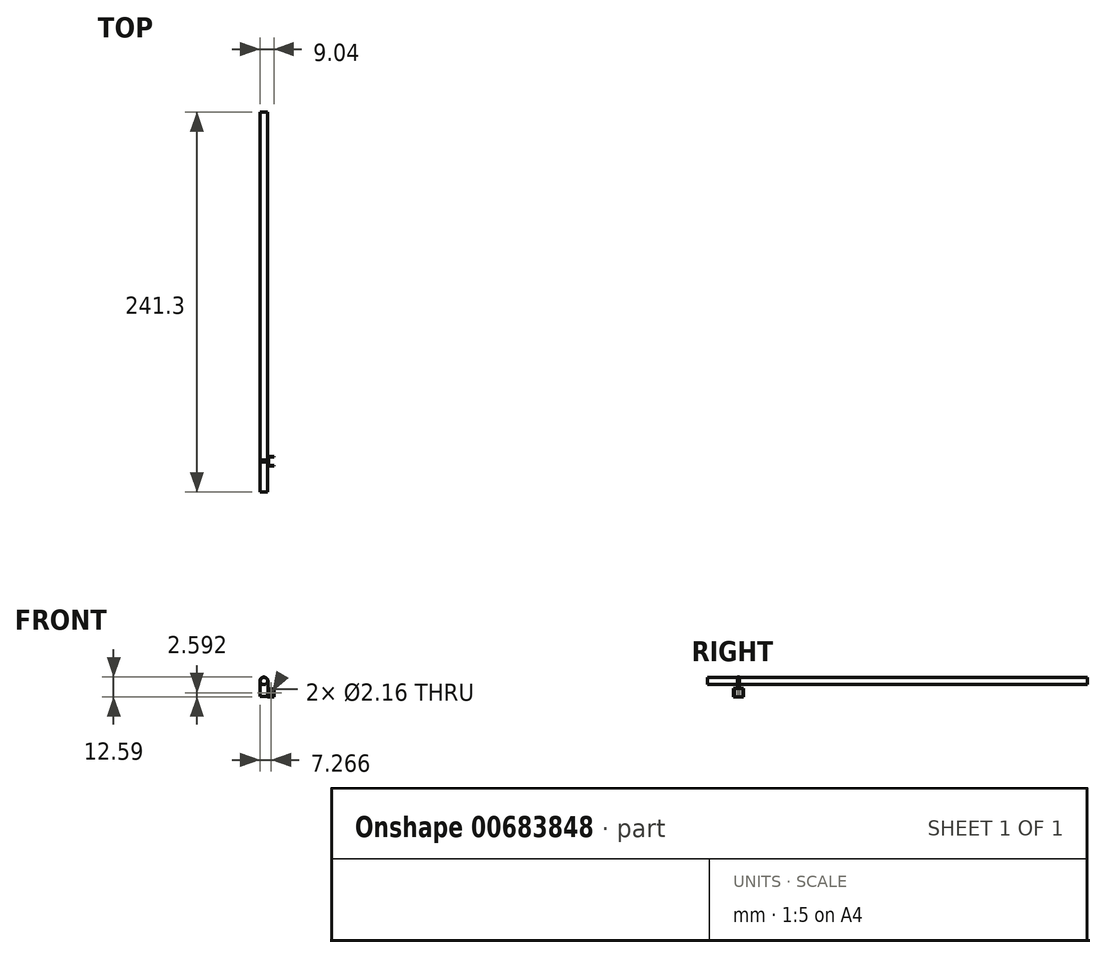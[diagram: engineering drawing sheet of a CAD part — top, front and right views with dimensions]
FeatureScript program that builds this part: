
annotation { "Feature Type Name" : "Feature", "Feature Type Description" : "" }
export const myFeature = defineFeature(function(context is Context, id is Id, definition is map)
    precondition{}
    {
        {
            var Q0;
            Q0=qCreatedBy(makeId("Front.planeOp"),FACE);
            var sketch = newSketch(context, id + "F0", { "sketchPlane" : qUnion([Q0])});
            skCircle(sketch, "E0", {"center": v(0, 5.4) * mm, "radius": 2.56 * mm});
            skArc(sketch, "E1", {"start": v(0, 2.56) * mm, "mid": v(-0.36, 2.53) * mm, "end": v(-0.72, 2.45) * mm});
            skLineSegment(sketch, "E2", {"start": v(2.56, 5.4) * mm, "end": v(2.56, 1.72) * mm});
            skLineSegment(sketch, "E3", {"start": v(-2.56, 5.4) * mm, "end": v(-2.56, 4.38) * mm});
            skArc(sketch, "E4.MirrorC", {"start": v(-11.6, 2.55) * mm, "mid": v(-11.6, 2.55) * mm, "end": v(-11.6, 2.55) * mm});
            skPoint(sketch, "E5.start.orphan", {"position": v(0, -2.56) * mm});
            skPoint(sketch, "E6.start.orphan", {"position": v(0, 2.56) * mm});
            skPoint(sketch, "E7.orphan", {"position": v(2.56, 0) * mm});
            skPoint(sketch, "E8.orphan", {"position": v(-2.56, 0) * mm});
            skLineSegment(sketch, "E9", {"start": v(-2.56, 4.38) * mm, "end": v(-2.56, -2.83) * mm});
            skLineSegment(sketch, "E10", {"start": v(2.56, 1.72) * mm, "end": v(2.52, -2.83) * mm});
            skPoint(sketch, "E10.endSnap0", {"position": v(2.44, 0.77) * mm});
            skPoint(sketch, "E11.start.orphan", {"position": v(2.56, 4.18) * mm});
            skLineSegment(sketch, "E12", {"start": v(-2.56, 5.4) * mm, "end": v(-2.56, -2.83) * mm});
            skPoint(sketch, "E13.end.orphan", {"position": v(2.44, -13.4) * mm});
            skLineSegment(sketch, "E14", {"start": v(-2.56, -2.83) * mm, "end": v(-2.56, -4.37) * mm});
            skLineSegment(sketch, "E15", {"start": v(2.52, -2.83) * mm, "end": v(2.52, -4.37) * mm});
            skLineSegment(sketch, "E16", {"start": v(-2.56, -4.37) * mm, "end": v(2.52, -4.37) * mm});
            skSolve(sketch);
        }
        {
            var Q0;
            {var subQ0=sQuery(id+"F0.wireOp",EDGE,"E0");var subQ1=makeQuery(id+"F0.imprint","INTERSECT",VERTEX,{"derivedFrom":[subQ0,sQuery(id+"F0.wireOp",EDGE,"E2")]});Q0=makeQuery(id+"F0.imprint","IMPRINT",FACE,{"disambiguationData":[TD([[makeQuery(id+"F0.imprint","IMPRINT",EDGE,{"disambiguationData":[TD([[subQ1,1.0]])],"derivedFrom":subQ0}),1.0]])]});}
            var Q1;
            {var subQ0=sQuery(id+"F0.wireOp",EDGE,"E3");Q1=makeQuery(id+"F0.imprint","IMPRINT",FACE,{"disambiguationData":[TD([[makeQuery(id+"F0.imprint","IMPRINT",EDGE,{"derivedFrom":subQ0}),1.0]])]});}
            var Q2;
            {var subQ0=sQuery(id+"F0.wireOp",EDGE,"E2");var subQ1=sQuery(id+"F0.wireOp",EDGE,"E1");var subQ2=makeQuery(id+"F0.imprint","INTERSECT",VERTEX,{"derivedFrom":[subQ1,subQ0]});Q2=makeQuery(id+"F0.imprint","IMPRINT",FACE,{"disambiguationData":[TD([[makeQuery(id+"F0.imprint","IMPRINT",EDGE,{"disambiguationData":[TD([[subQ2,-1.0]])],"derivedFrom":subQ1}),-1.0]])]});}
            var Q3;
            {var subQ0=sQuery(id+"F0.wireOp",EDGE,"E1");var subQ1=makeQuery(id+"F0.imprint","INTERSECT",VERTEX,{"derivedFrom":[subQ0,sQuery(id+"F0.wireOp",EDGE,"E3")]});Q3=makeQuery(id+"F0.imprint","IMPRINT",FACE,{"disambiguationData":[TD([[makeQuery(id+"F0.imprint","IMPRINT",EDGE,{"disambiguationData":[TD([[subQ1,1.0]])],"derivedFrom":subQ0}),1.0]])]});}
            var Q4;
            {var subQ0=sQuery(id+"F0.wireOp",EDGE,"263fcdb8-d820-4d45-9f7c-0084accf3f070.MirrorCS");Q4=makeQuery(id+"F0.imprint","IMPRINT",FACE,{"disambiguationData":[TD([[makeQuery(id+"F0.imprint","IMPRINT",EDGE,{"derivedFrom":subQ0}),1.0]])]});}
            var Q5;
            {var subQ0=sQuery(id+"F0.wireOp",EDGE,"nn3kji8N-mWU8-6sac-MlCo-DN8aCnxxy875");Q5=makeQuery(id+"F0.imprint","IMPRINT",FACE,{"disambiguationData":[TD([[makeQuery(id+"F0.imprint","IMPRINT",EDGE,{"derivedFrom":subQ0}),-1.0]])]});}
            var Q6;
            {var subQ1=sQuery(id+"F0.wireOp",EDGE,"nn3kji8N-mWU8-6sac-MlCo-DN8aCnxxy875");Q6=makeQuery(id+"F0.imprint","IMPRINT",FACE,{"disambiguationData":[TD([[makeQuery(id+"F0.imprint","IMPRINT",EDGE,{"derivedFrom":subQ1}),1.0]])]});}
            var Q7;
            {var subQ0=sQuery(id+"F0.wireOp",EDGE,"G4lSKCHw-J7V3-nXiF-vaOj-cBAkdTGiRsgI");var subQ1=sQuery(id+"F0.wireOp",EDGE,"E2");var subQ2=makeQuery(id+"F0.imprint","INTERSECT",VERTEX,{"derivedFrom":[subQ1,subQ0]});Q7=makeQuery(id+"F0.imprint","IMPRINT",FACE,{"disambiguationData":[TD([[makeQuery(id+"F0.imprint","IMPRINT",EDGE,{"disambiguationData":[TD([[subQ2,-1.0]])],"derivedFrom":subQ1}),-1.0]])]});}
            var Q8;
            {var subQ1=sQuery(id+"F0.wireOp",EDGE,"cd80d73e-9bc2-4dc0-84be-316595012ded0.MirrorCS");Q8=makeQuery(id+"F0.imprint","IMPRINT",FACE,{"disambiguationData":[TD([[makeQuery(id+"F0.imprint","IMPRINT",EDGE,{"derivedFrom":subQ1}),-1.0]])]});}
            var Q9;
            {var subQ0=sQuery(id+"F0.wireOp",EDGE,"E2");var subQ1=sQuery(id+"F0.wireOp",EDGE,"E1");var subQ2=makeQuery(id+"F0.imprint","INTERSECT",VERTEX,{"derivedFrom":[subQ1,subQ0]});Q9=makeQuery(id+"F0.imprint","IMPRINT",FACE,{"disambiguationData":[TD([[makeQuery(id+"F0.imprint","IMPRINT",EDGE,{"disambiguationData":[TD([[subQ2,1.0]])],"derivedFrom":subQ1}),-1.0]])]});}
            var Q10;
            {var subQ0=sQuery(id+"F0.wireOp",EDGE,"kcDJH2sf-21BA-L9Yy-qe85-3mtlSAZsPEdo");Q10=makeQuery(id+"F0.imprint","IMPRINT",FACE,{"disambiguationData":[TD([[makeQuery(id+"F0.imprint","IMPRINT",EDGE,{"derivedFrom":subQ0}),1.0]])]});}
            var Q11;
            {var subQ0=sQuery(id+"F0.wireOp",EDGE,"WZRXunty-gl11-gvDB-eq7a-ggUTLZATC6E6");Q11=makeQuery(id+"F0.imprint","IMPRINT",FACE,{"disambiguationData":[TD([[makeQuery(id+"F0.imprint","IMPRINT",EDGE,{"derivedFrom":subQ0}),1.0]])]});}
            var Q12;
            {var subQ6=sQuery(id+"F0.wireOp",EDGE,"E9");Q12=makeQuery(id+"F0.imprint","IMPRINT",FACE,{"disambiguationData":[TD([[makeQuery(id+"F0.imprint","IMPRINT",EDGE,{"derivedFrom":subQ6}),1.0]])]});}
            var Q13;
            {var subQ3=sQuery(id+"F0.wireOp",EDGE,"mmOzPl4o-ixsb-ohx5-I9sC-uw6xFzwwk5XC");Q13=makeQuery(id+"F0.imprint","IMPRINT",FACE,{"disambiguationData":[TD([[makeQuery(id+"F0.imprint","IMPRINT",EDGE,{"derivedFrom":subQ3}),1.0]])]});}
            extrude(context, id + "F1", {"entities" : qUnion([Q0, Q1, Q2, Q3, Q4, Q5, Q6, Q7, Q8, Q9, Q10, Q11, Q12, Q13]), "oppositeDirection" : true, "depth" : 1.27 * mm, "offsetDistance" : 25.4 * mm});
        }
        {
            var Q0;
            Q0=makeQuery(id+"F1.opExtrude","CAP_FACE",FACE,{"disambiguationData":[OSD([sQuery(id+"F0.wireOp",EDGE,"NQC7D4eD-zXav-Hkey-WBNL-hidIfPrPsmmw"),sQuery(id+"F0.wireOp",EDGE,"Y8T2P4YK-4LtQ-yw2D-mTcZ-RdnlM3RRqPwx"),sQuery(id+"F0.wireOp",EDGE,"ErvJBt9r-b4Zx-H6VP-9QHq-hFwdqEP6Mpm7"),sQuery(id+"F0.wireOp",EDGE,"E0")])],"isStart":false});
            var sketch = newSketch(context, id + "F2", { "sketchPlane" : qUnion([Q0])});
            skCircle(sketch, "E17", {"center": v(0, 5.4) * mm, "radius": 2.29 * mm});
            skSolve(sketch);
        }
        {
            var Q0;
            Q0=makeQuery(id+"F2.imprint","IMPRINT",FACE,{"disambiguationData":[TD([[makeQuery(id+"F2.imprint","IMPRINT",EDGE,{"derivedFrom":sQuery(id+"F2.wireOp",EDGE,"E17")}),1.0]])]});
            extrude(context, id + "F3", {"entities" : qUnion([Q0]), "operationType" : NewBodyOperationType.ADD, "depth" : 220.98 * mm, "offsetDistance" : 25.4 * mm, "hasSecondDirection" : true, "secondDirectionOppositeDirection" : true, "secondDirectionDepth" : 20.32 * mm});
        }
        {
            var Q0;
            Q0=makeQuery(id+"F1.opExtrude","SWEPT_FACE",FACE,{"disambiguationData":[OSD([sQuery(id+"F0.wireOp",EDGE,"E10")])]});
            var sketch = newSketch(context, id + "F4", { "sketchPlane" : qUnion([Q0])});
            skLineSegment(sketch, "E18.bottom", {"start": v(3.66, -4.58) * mm, "end": v(-2.5, -4.58) * mm});
            skLineSegment(sketch, "E18.top", {"start": v(3.66, 0.6) * mm, "end": v(-2.5, 0.6) * mm});
            skLineSegment(sketch, "E18.left", {"start": v(3.66, -4.58) * mm, "end": v(3.66, 0.6) * mm});
            skLineSegment(sketch, "E18.right", {"start": v(-2.5, -4.58) * mm, "end": v(-2.5, 0.6) * mm});
            skPoint(sketch, "E18.middle.positionSnap0", {"position": v(0, 0) * mm});
            skPoint(sketch, "E18.centerSnap0", {"position": v(0, 0) * mm});
            skSolve(sketch);
        }
        {
            var Q0;
            {var subQ0=sQuery(id+"F4.wireOp",EDGE,"E18.left");Q0=makeQuery(id+"F4.imprint","IMPRINT",FACE,{"disambiguationData":[TD([[makeQuery(id+"F4.imprint","IMPRINT",EDGE,{"derivedFrom":subQ0}),1.0]])]});}
            var Q1;
            {var subQ0=sQuery(id+"F4.wireOp",EDGE,"E18.right");Q1=makeQuery(id+"F4.imprint","IMPRINT",FACE,{"disambiguationData":[TD([[makeQuery(id+"F4.imprint","IMPRINT",EDGE,{"derivedFrom":subQ0}),-1.0]])]});}
            var Q2;
            {var subQ1=sQuery(id+"F0.wireOp",EDGE,"0STaALuz-qcVV-emnR-7TsT-yvQYUWInrF14");var subQ6=makeQuery(id+"F1.opExtrude","SWEPT_EDGE",EDGE,{"disambiguationData":[OSD([sQuery(id+"F0.wireOp",EDGE,"WZRXunty-gl11-gvDB-eq7a-ggUTLZATC6E6"),subQ1,sQuery(id+"F0.wireOp",EDGE,"E11")])]});Q2=makeQuery(id+"F4.imprint","IMPRINT",FACE,{"disambiguationData":[TD([[makeQuery(id+"F4.imprint","IMPRINT",EDGE,{"derivedFrom":subQ6}),1.0]])]});}
            var Q3;
            {var subQ0=sQuery(id+"F4.wireOp",EDGE,"E18.bottom");var subQ1=sQuery(id+"F0.wireOp",EDGE,"0STaALuz-qcVV-emnR-7TsT-yvQYUWInrF14");var subQ2=makeQuery(id+"F1.opExtrude","CAP_EDGE",EDGE,{"disambiguationData":[OSD([subQ1])],"isStart":false});var subQ3=makeQuery(id+"F4.imprint","INTERSECT",VERTEX,{"derivedFrom":[subQ2,subQ0]});Q3=makeQuery(id+"F4.imprint","IMPRINT",FACE,{"disambiguationData":[TD([[makeQuery(id+"F4.imprint","IMPRINT",EDGE,{"disambiguationData":[TD([[subQ3,-1.0]])],"derivedFrom":subQ0}),-1.0]])]});}
            var Q4;
            {var subQ1=sQuery(id+"F0.wireOp",EDGE,"0STaALuz-qcVV-emnR-7TsT-yvQYUWInrF14");var subQ6=makeQuery(id+"F1.opExtrude","SWEPT_EDGE",EDGE,{"disambiguationData":[OSD([subQ1,sQuery(id+"F0.wireOp",EDGE,"YwyUZhCz-AFjn-tTO7-jNPe-idEtptmNyLsH")])]});Q4=makeQuery(id+"F4.imprint","IMPRINT",FACE,{"disambiguationData":[TD([[makeQuery(id+"F4.imprint","IMPRINT",EDGE,{"derivedFrom":subQ6}),-1.0]])]});}
            var Q5;
            {var subQ1=sQuery(id+"F0.wireOp",EDGE,"E10");var subQ6=makeQuery(id+"F1.opExtrude","SWEPT_EDGE",EDGE,{"disambiguationData":[OSD([subQ1,sQuery(id+"F0.wireOp",EDGE,"mmOzPl4o-ixsb-ohx5-I9sC-uw6xFzwwk5XC")])]});Q5=makeQuery(id+"F4.imprint","IMPRINT",FACE,{"disambiguationData":[TD([[makeQuery(id+"F4.imprint","IMPRINT",EDGE,{"derivedFrom":subQ6}),-1.0]])]});}
            extrude(context, id + "F5", {"entities" : qUnion([Q0, Q1, Q2, Q3, Q4, Q5]), "depth" : 3.94 * mm, "offsetDistance" : 25.4 * mm});
        }
        {
            var Q0;
            Q0=makeQuery(id+"F5.opExtrude","CAP_FACE",FACE,{"disambiguationData":[OSD([sQuery(id+"F0.wireOp",EDGE,"WZRXunty-gl11-gvDB-eq7a-ggUTLZATC6E6"),sQuery(id+"F0.wireOp",EDGE,"0STaALuz-qcVV-emnR-7TsT-yvQYUWInrF14"),sQuery(id+"F0.wireOp",EDGE,"E11"),sQuery(id+"F4.wireOp",EDGE,"E18.bottom"),sQuery(id+"F4.wireOp",EDGE,"E18.top"),sQuery(id+"F4.wireOp",EDGE,"E18.left"),sQuery(id+"F4.wireOp",EDGE,"E18.right")])],"isStart":false});
            var Q1;
            {var subQ0=sQuery(id+"F4.wireOp",EDGE,"E18.top");Q1=makeQuery(id+"F5.opExtrude","SWEPT_FACE",FACE,{"disambiguationData":[OSD([subQ0]),TDD([makeQuery(id+"F4.imprint","IMPRINT",EDGE,{"disambiguationData":[TD([[makeQuery(id+"F4.imprint","INTERSECT",VERTEX,{"derivedFrom":[subQ0,sQuery(id+"F4.wireOp",EDGE,"E18.left")]}),-1.0]])],"derivedFrom":subQ0})])]});}
            var Q2;
            {var subQ0=sQuery(id+"F4.wireOp",EDGE,"E18.top");Q2=makeQuery(id+"F5.opExtrude","SWEPT_FACE",FACE,{"disambiguationData":[OSD([subQ0]),TDD([makeQuery(id+"F4.imprint","IMPRINT",EDGE,{"disambiguationData":[TD([[makeQuery(id+"F4.imprint","INTERSECT",VERTEX,{"derivedFrom":[subQ0,sQuery(id+"F4.wireOp",EDGE,"E18.right")]}),1.0]])],"derivedFrom":subQ0})])]});}
            var Q3;
            Q3=makeQuery(id+"F5.opExtrude","SWEPT_FACE",FACE,{"disambiguationData":[OSD([sQuery(id+"F4.wireOp",EDGE,"E18.bottom")])]});
            var Q4;
            Q4=makeQuery(id+"F5.opExtrude","SWEPT_FACE",FACE,{"disambiguationData":[OSD([sQuery(id+"F0.wireOp",EDGE,"WZRXunty-gl11-gvDB-eq7a-ggUTLZATC6E6"),sQuery(id+"F0.wireOp",EDGE,"0STaALuz-qcVV-emnR-7TsT-yvQYUWInrF14"),sQuery(id+"F0.wireOp",EDGE,"E11")])]});
            shell(context, id + "F6", {"entities" : qUnion([Q0, Q1, Q2, Q3, Q4]), "thickness" : 0.38 * mm});
        }
        {
            var Q0;
            Q0=makeQuery(id+"F5.opExtrude","SWEPT_FACE",FACE,{"disambiguationData":[OSD([sQuery(id+"F4.wireOp",EDGE,"E18.right")])]});
            var sketch = newSketch(context, id + "F7", { "sketchPlane" : qUnion([Q0])});
            skCircle(sketch, "E19", {"center": v(4.7, -2.04) * mm, "radius": 1.08 * mm});
            skSolve(sketch);
        }
        {
            var Q0;
            Q0 = qSketchRegion(id + "F7", true);
            extrude(context, id + "F8", {"entities" : qUnion([Q0]), "operationType" : NewBodyOperationType.REMOVE, "oppositeDirection" : true, "depth" : 11.18 * mm, "offsetDistance" : 25.4 * mm});
        }
    });
